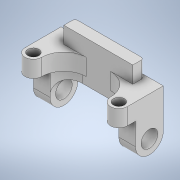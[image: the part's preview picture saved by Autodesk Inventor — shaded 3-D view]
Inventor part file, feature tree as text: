
AUTODESK INVENTOR PART (.ipt)
format: ipt  version: 2022 (Build 260153000, 153)  size: 207,360 bytes
history: native  units: mm
features: extrude x4, sketch x4, fillet x2, mirror x1
ambient origin geometry x8: Origin, YZ Plane, XZ Plane, XY Plane, X Axis, Y Axis, Z Axis, Center Point
bodies: Solid1 (feature_tree)
feature tree (11):
  extrude  "Extrusion1"  Depth=3.0mm
  extrude  "Extrusion2"  Depth=4.0mm
  extrude  "Extrusion3"  Depth=1.5mm
  extrude  "Extrusion4"  Depth=3.5mm TaperAngle=0.0deg
  fillet  "Fillet1"  Radius=2.0mm
  fillet  "Fillet2"  Radius=1.0mm
  mirror  "Mirror1"
  sketch  "Sketch1"  dims[d4=2.0mm d5=3.0mm]
  sketch  "Sketch2"  dims[d8=8.0mm d9=4.0mm]
  sketch  "Sketch3"  dims[d10=1.5mm d11=1.5mm]
  sketch  "Sketch4"  dims[d12=2.5mm d13=3.0mm d14=0.0mm d15=2.0mm d16=1.0mm d17=0.5mm d18=3.0mm d19=0.0mm d20=5.0mm d21=3.0mm d22=2.5mm d23=4.0mm d24=3.0mm d25=0.0mm d26=5.2mm d27=3.0mm d28=0.0mm d29=4.0mm d30=3.5mm]
